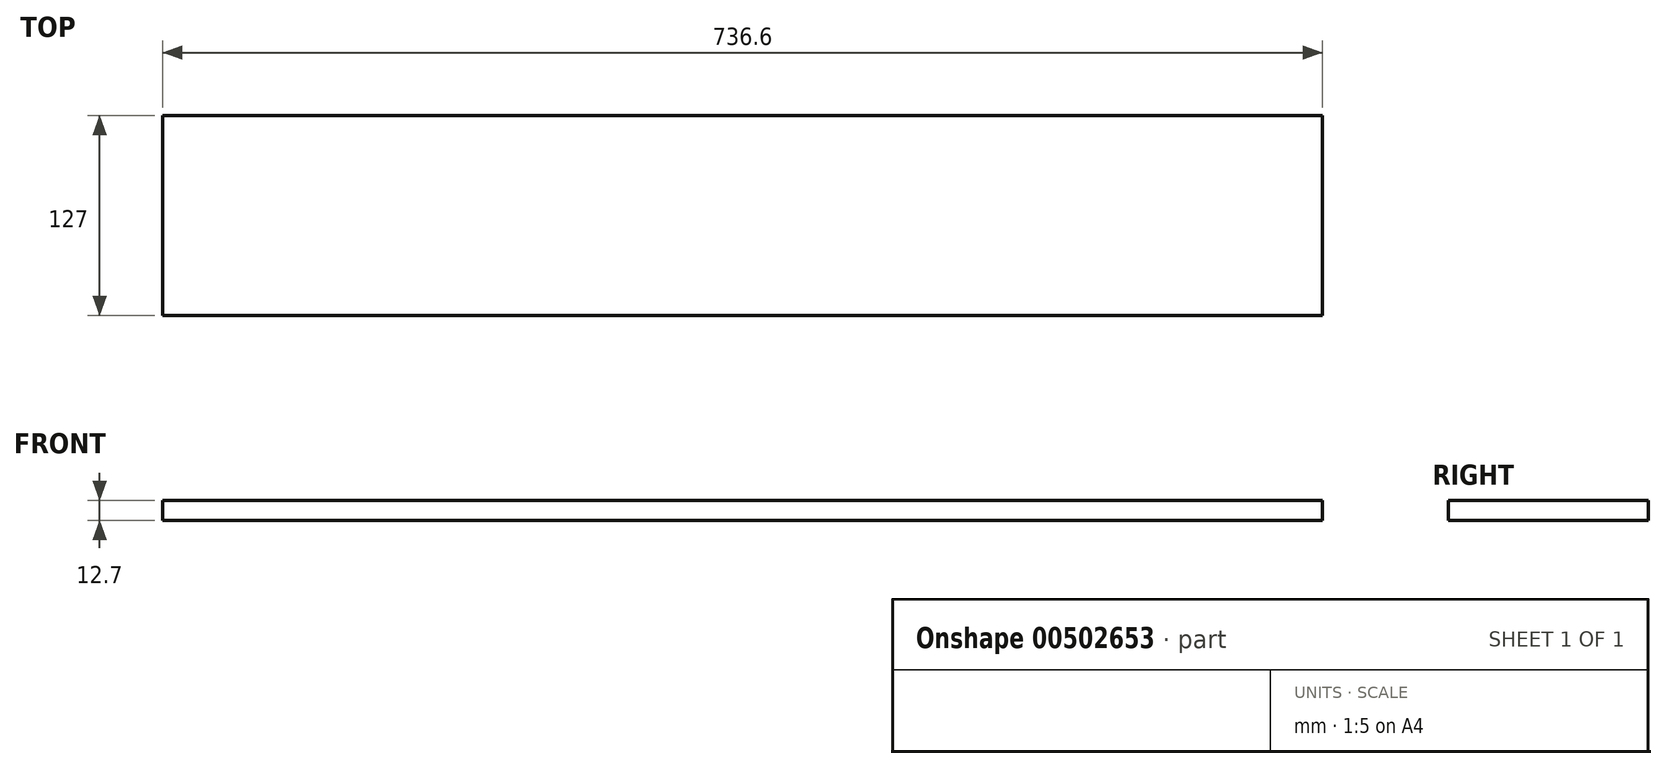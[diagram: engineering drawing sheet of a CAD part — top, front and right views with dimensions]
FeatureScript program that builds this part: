
annotation { "Feature Type Name" : "Feature", "Feature Type Description" : "" }
export const myFeature = defineFeature(function(context is Context, id is Id, definition is map)
    precondition{}
    {
        {
            var Q0;
            Q0=qCreatedBy(makeId("Front.planeOp"),FACE);
            var sketch = newSketch(context, id + "F0", { "sketchPlane" : qUnion([Q0])});
            skLineSegment(sketch, "E0.bottom", {"start": v(-374.98, -19.96) * mm, "end": v(361.62, -19.96) * mm});
            skLineSegment(sketch, "E0.top", {"start": v(-374.98, -32.66) * mm, "end": v(361.62, -32.66) * mm});
            skLineSegment(sketch, "E0.left", {"start": v(-374.98, -19.96) * mm, "end": v(-374.98, -32.66) * mm});
            skLineSegment(sketch, "E0.right", {"start": v(361.62, -19.96) * mm, "end": v(361.62, -32.66) * mm});
            skSolve(sketch);
        }
        {
            var Q0;
            Q0=makeQuery(id+"F0.imprint","IMPRINT",FACE,{"disambiguationData":[TD([[makeQuery(id+"F0.imprint","IMPRINT",EDGE,{"derivedFrom":sQuery(id+"F0.wireOp",EDGE,"E0.bottom")}),-1.0]])]});
            extrude(context, id + "F1", {"entities" : qUnion([Q0]), "depth" : 127 * mm});
        }
    });
